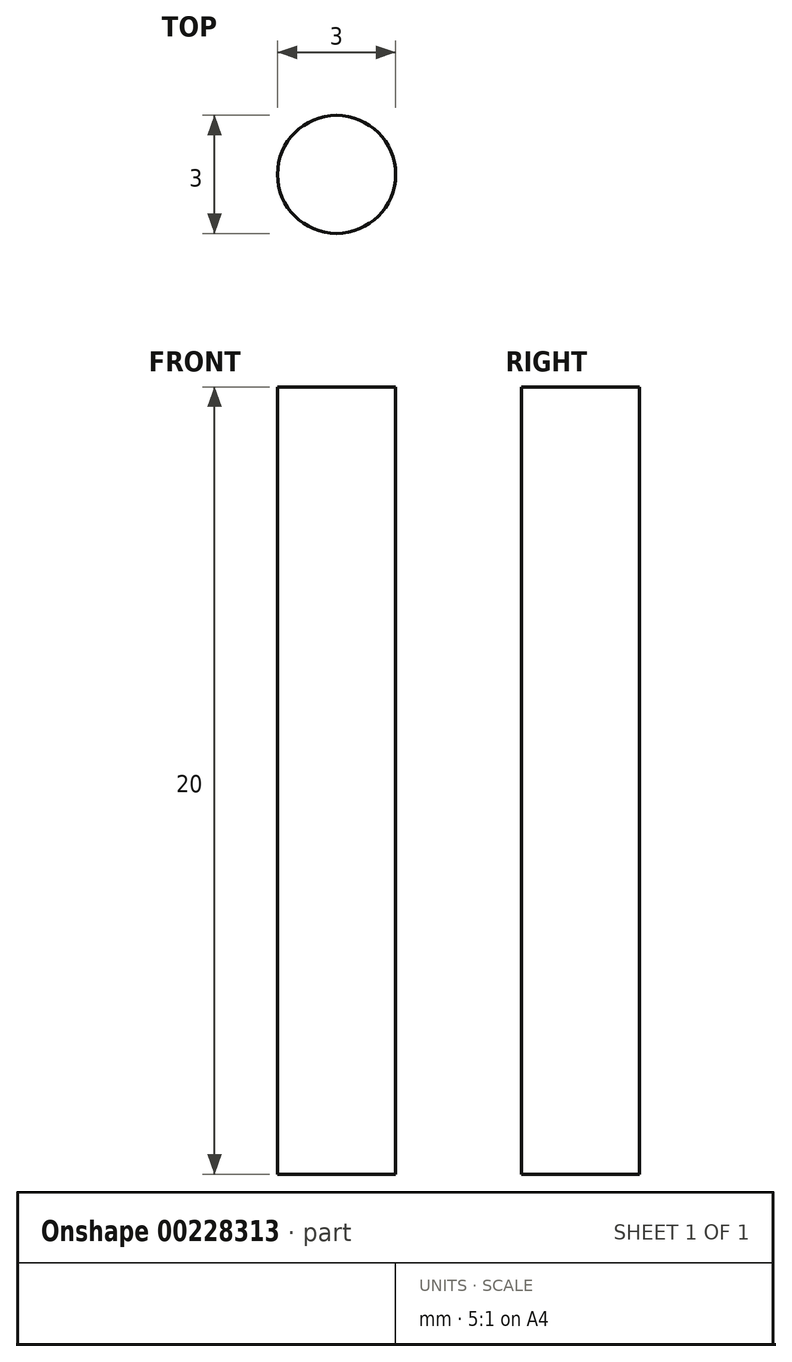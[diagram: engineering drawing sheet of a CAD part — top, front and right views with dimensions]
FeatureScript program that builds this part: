
annotation { "Feature Type Name" : "Feature", "Feature Type Description" : "" }
export const myFeature = defineFeature(function(context is Context, id is Id, definition is map)
    precondition{}
    {
        {
            var Q0;
            Q0=qCreatedBy(makeId("Top.planeOp"),FACE);
            var sketch = newSketch(context, id + "F0", { "sketchPlane" : qUnion([Q0])});
            skCircle(sketch, "E0", {"center": v(-36.66, 24.47) * mm, "radius": 1.5 * mm});
            skSolve(sketch);
        }
        {
            var Q0;
            Q0=makeQuery(id+"F0.imprint","IMPRINT",FACE,{"disambiguationData":[TD([[makeQuery(id+"F0.imprint","IMPRINT",EDGE,{"derivedFrom":sQuery(id+"F0.wireOp",EDGE,"E0")}),1.0]])]});
            extrude(context, id + "F1", {"entities" : qUnion([Q0]), "depth" : 20 * mm});
        }
    });
